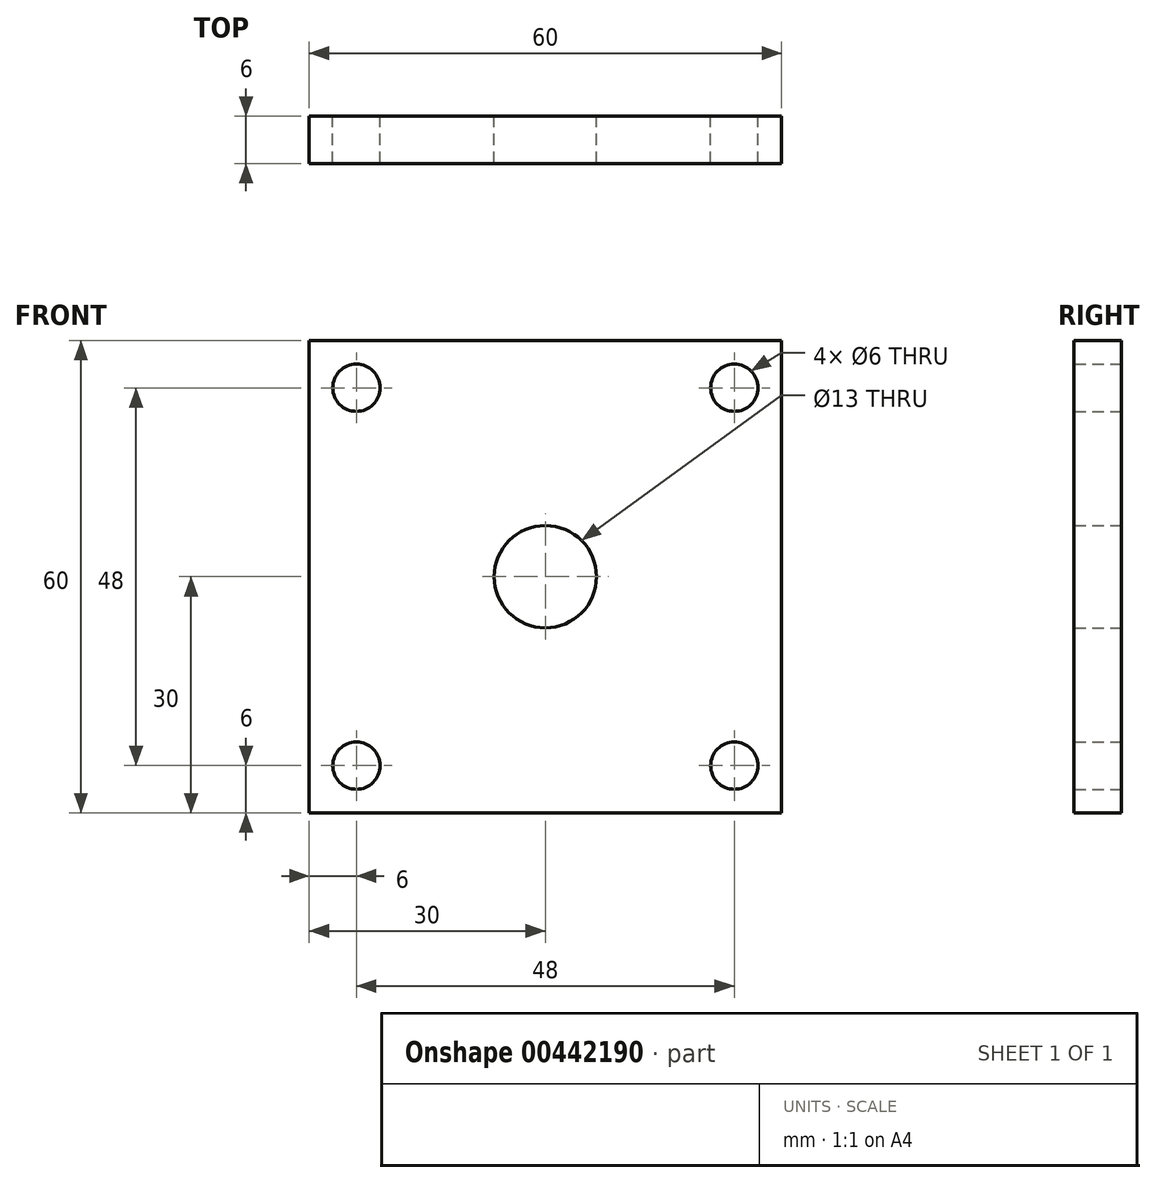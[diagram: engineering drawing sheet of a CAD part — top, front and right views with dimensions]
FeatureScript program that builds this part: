
annotation { "Feature Type Name" : "Feature", "Feature Type Description" : "" }
export const myFeature = defineFeature(function(context is Context, id is Id, definition is map)
    precondition{}
    {
        {
            var Q0;
            Q0=qCreatedBy(makeId("Front.planeOp"),FACE);
            var sketch = newSketch(context, id + "F0", { "sketchPlane" : qUnion([Q0])});
            skLineSegment(sketch, "E0.bottom", {"start": v(30, 30) * mm, "end": v(-30, 30) * mm});
            skLineSegment(sketch, "E0.top", {"start": v(30, -30) * mm, "end": v(-30, -30) * mm});
            skLineSegment(sketch, "E0.left", {"start": v(30, 30) * mm, "end": v(30, -30) * mm});
            skLineSegment(sketch, "E0.right", {"start": v(-30, 30) * mm, "end": v(-30, -30) * mm});
            skPoint(sketch, "E0.middle", {"position": v(0, 0) * mm});
            skCircle(sketch, "E1", {"center": v(-24, 24) * mm, "radius": 3 * mm});
            skCircle(sketch, "E2", {"center": v(24, 24) * mm, "radius": 3 * mm});
            skCircle(sketch, "E3", {"center": v(24, -24) * mm, "radius": 3 * mm});
            skCircle(sketch, "E4", {"center": v(-24, -24) * mm, "radius": 3 * mm});
            skCircle(sketch, "E5", {"center": v(0, 0) * mm, "radius": 6.5 * mm});
            skSolve(sketch);
        }
        {
            var Q0;
            Q0=makeQuery(id+"F0.imprint","IMPRINT",FACE,{"disambiguationData":[TD([[makeQuery(id+"F0.imprint","IMPRINT",EDGE,{"derivedFrom":sQuery(id+"F0.wireOp",EDGE,"E0.bottom")}),1.0]])]});
            extrude(context, id + "F1", {"entities" : qUnion([Q0]), "depth" : 6 * mm});
        }
    });
